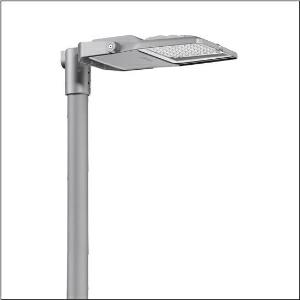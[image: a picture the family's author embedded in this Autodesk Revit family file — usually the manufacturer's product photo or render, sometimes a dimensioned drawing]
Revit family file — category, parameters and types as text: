
# Revit family: floodlight_fl_21_mini___pl61_5xa7775c2c3a_8aba
name_source: partatom
category: Lighting Fixtures
units: mm (PartAtom-declared; Revit-internal decimal feet)

## family parameters
Cut with Voids When Loaded = No
Host = Face
Light Source = No
Part Type = Normal
Room Calculation Point = No
Round Connector Dimension = Use Diameter
Shared = No

## types (1)
- --- (1 x LED, 11960 lm, 89 W, 3000K)
    Apparent Load = 89 VA
    CIE Flux Codes = 33 65 98 100 100
    Color Rendering = 70
    Color Temperature = 3000K
    Default Elevation = 1800 mm
    Description = Floodlight FL 21 mini, floodlight, primary light control with lens, of PMMA, primary optical cover: protective disc, of toughened safety glass, transparent, light distribution: PL61, light emission: direct distribution, installation type: surface-mounted, LED, High Power LED, rated luminous flux: 11.960lm, luminous efficacy: 134lm/W, light colour: 730, colour temperature: 3000K, control: flexible luminous flux parameterisation, time-dependent luminous flux control, constant luminous flux control, overheat protection, presetting dimming logarithmic, with terminal, 6-pole, mains connection: 220..240V, AC, 50/60Hz, start of lifetime: 89W, end of service life: 94W, reduction: 43W, luminaire housing, of diecast aluminium, powder-coated, Siteco® metallic grey (DB 702S), corrosivity category C5 mid according to DIN EN ISO 12944, sealing non-destructively replaceable, please order mast flange separately, mast bracket, of steel, galvanised, powder-coated, Siteco® metallic grey (DB 702S), Smart Interface above, protection rating (complete): IP66, insulation class (complete): insulation class II (safety insulation), certification: CE, ENEC, VDE, protection symbol: D, impact resistance: IK08, permissible operating ambient temperature: -40..+40°C, permissible operating ambient temperature for outdoor applications: -40..+50°C, standard: DIN EN 12944, LABS conformity tested according to VDMA 24364:2018-05, packaging unit: 1 piece

Light Distribution: PL61
    Height = 70 mm
    Lamp = 1 x LED
    Lamp Light Flux = 11960 lm
    Lamp Power = 89 W
    Lamp count = 1
    Length = 485 mm
    Luminous efficacy = 134 lm/W
    Manufacturer = Siteco
    ModVariant = No
    Model = 5XA7775C2C3A
    Number of Poles = 1
    OnlyDefault = Yes
    Power Factor = 1
    Product Name = Floodlight FL 21 mini | PL61
    Product group = floodlight | pylon annexe
    ProductGroupID = 6200
    Protection Class = Protection class II
    Protection Degree = IP 66
    RLX_Detail_Level = 1
    RLX_Emergency_Light_Flux = 0 lm
    RLX_Emergency_Type = 0
    RLX_Emergency_Type_DB = No
    RlxData = <blob elided: 100957 chars, md5=747aef72>
    Socket = socket
    Standby Power = 0 W
    System Light Flux = 11960 lm
    System Power = 89 W
    Type Comments = factory setting: luminous flux: 100 % | dim-lin: 254 | 456 mA
    Type Image = l_1007125.jpg
    URL = http://relux.com
    VarID = @adj_105137
    Voltage = 0 V
    Weight = 0.00 kg
    Width = 337 mm

## geometry (parser evidence)
native form markers: Blend x4, Sweep x14
no freeform markers — native parametric forms only
